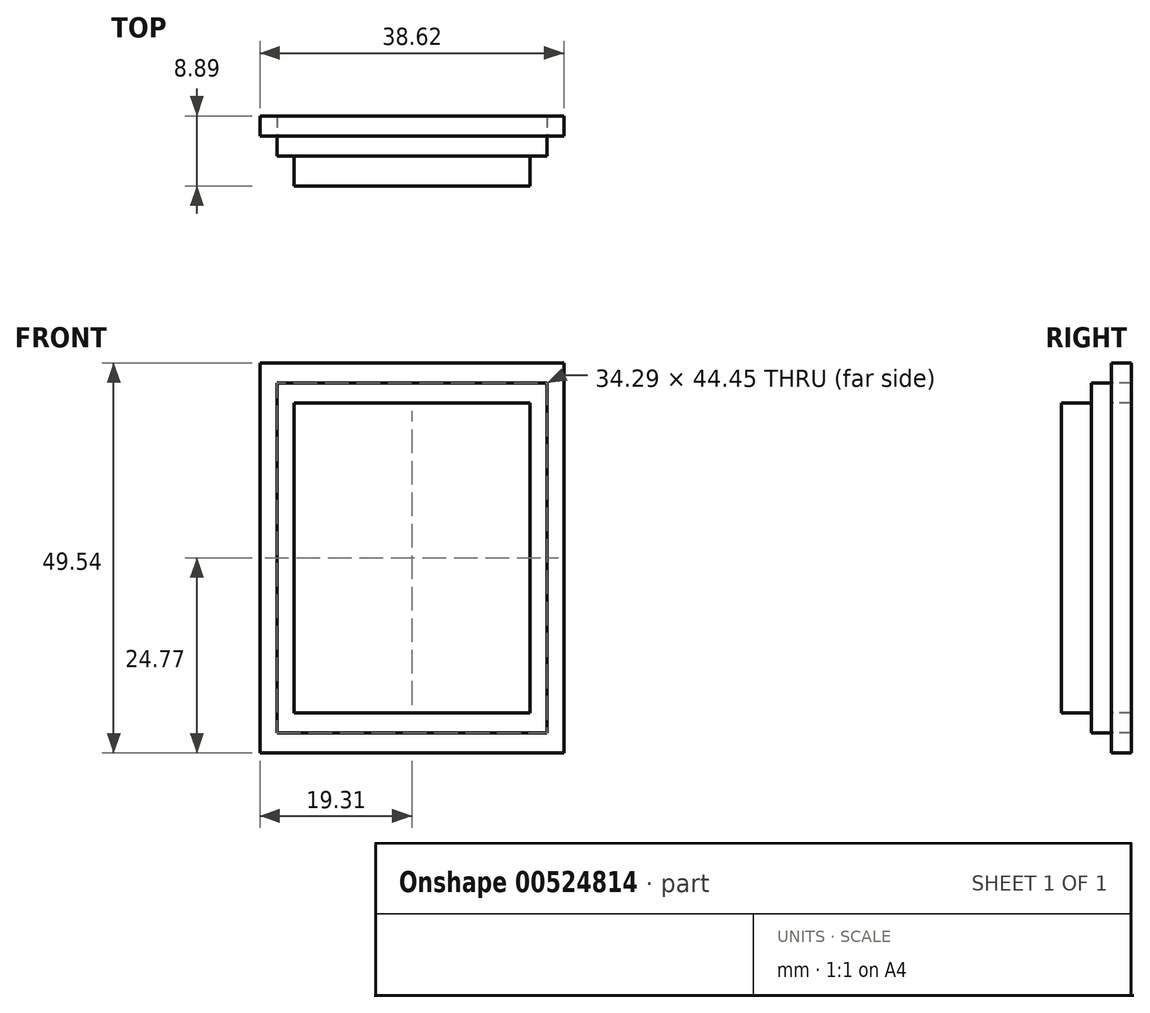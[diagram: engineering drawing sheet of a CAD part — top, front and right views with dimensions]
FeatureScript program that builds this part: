
annotation { "Feature Type Name" : "Feature", "Feature Type Description" : "" }
export const myFeature = defineFeature(function(context is Context, id is Id, definition is map)
    precondition{}
    {
        {
            var Q0;
            Q0=qCreatedBy(makeId("Front.planeOp"),FACE);
            var sketch = newSketch(context, id + "F0", { "sketchPlane" : qUnion([Q0])});
            skLineSegment(sketch, "E0.bottom", {"start": v(17.14, -22.23) * mm, "end": v(-17.14, -22.23) * mm});
            skLineSegment(sketch, "E0.top", {"start": v(17.14, 22.23) * mm, "end": v(-17.14, 22.23) * mm});
            skLineSegment(sketch, "E0.left", {"start": v(17.14, -22.23) * mm, "end": v(17.14, 22.23) * mm});
            skLineSegment(sketch, "E0.right", {"start": v(-17.14, -22.23) * mm, "end": v(-17.14, 22.23) * mm});
            skPoint(sketch, "E0.middle", {"position": v(0, 0) * mm});
            skLineSegment(sketch, "E1.bottom", {"start": v(-14.98, -22.23) * mm, "end": v(-19.31, -22.23) * mm});
            skLineSegment(sketch, "E1.top", {"start": v(-14.98, 22.23) * mm, "end": v(-19.31, 22.23) * mm});
            skLineSegment(sketch, "E1.left", {"start": v(-14.98, -22.23) * mm, "end": v(-14.98, 22.23) * mm});
            skLineSegment(sketch, "E1.right", {"start": v(-19.31, -22.23) * mm, "end": v(-19.31, 22.23) * mm});
            skPoint(sketch, "E1.middle", {"position": v(-17.14, 0) * mm});
            skLineSegment(sketch, "E2.bottom", {"start": v(19.31, -22.23) * mm, "end": v(14.98, -22.23) * mm});
            skLineSegment(sketch, "E2.top", {"start": v(19.31, 22.23) * mm, "end": v(14.98, 22.23) * mm});
            skLineSegment(sketch, "E2.left", {"start": v(19.31, -22.23) * mm, "end": v(19.31, 22.23) * mm});
            skLineSegment(sketch, "E2.right", {"start": v(14.98, -22.23) * mm, "end": v(14.98, 22.23) * mm});
            skPoint(sketch, "E2.middle", {"position": v(17.15, 0) * mm});
            skLineSegment(sketch, "E3.bottom", {"start": v(19.31, 19.69) * mm, "end": v(-19.31, 19.69) * mm});
            skLineSegment(sketch, "E3.top", {"start": v(19.31, 24.77) * mm, "end": v(-19.31, 24.77) * mm});
            skLineSegment(sketch, "E3.left", {"start": v(19.31, 19.69) * mm, "end": v(19.31, 24.77) * mm});
            skLineSegment(sketch, "E3.right", {"start": v(-19.31, 19.69) * mm, "end": v(-19.31, 24.77) * mm});
            skPoint(sketch, "E3.middle", {"position": v(0, 22.23) * mm});
            skLineSegment(sketch, "E4.bottom", {"start": v(19.31, -24.77) * mm, "end": v(-19.31, -24.77) * mm});
            skLineSegment(sketch, "E4.top", {"start": v(19.31, -19.68) * mm, "end": v(-19.31, -19.68) * mm});
            skLineSegment(sketch, "E4.left", {"start": v(19.31, -24.77) * mm, "end": v(19.31, -19.68) * mm});
            skLineSegment(sketch, "E4.right", {"start": v(-19.31, -24.77) * mm, "end": v(-19.31, -19.68) * mm});
            skPoint(sketch, "E4.middle", {"position": v(0, -22.23) * mm});
            skSolve(sketch);
        }
        {
            var Q0;
            {var subQ0=sQuery(id+"F0.wireOp",EDGE,"E4.top");var subQ1=sQuery(id+"F0.wireOp",EDGE,"E1.left");var subQ2=makeQuery(id+"F0.imprint","INTERSECT",VERTEX,{"derivedFrom":[subQ1,subQ0]});Q0=makeQuery(id+"F0.imprint","IMPRINT",FACE,{"disambiguationData":[TD([[makeQuery(id+"F0.imprint","IMPRINT",EDGE,{"disambiguationData":[TD([[subQ2,-1.0]])],"derivedFrom":subQ1}),-1.0]])]});}
            extrude(context, id + "F1", {"entities" : qUnion([Q0]), "depth" : 6.35 * mm, "offsetDistance" : 25.4 * mm});
        }
        {
            var Q0;
            Q0 = qSketchRegion(id + "F0", true);
            extrude(context, id + "F2", {"entities" : qUnion([Q0]), "oppositeDirection" : true, "depth" : 2.54 * mm, "offsetDistance" : 25.4 * mm});
        }
        {
            var Q0;
            {var subQ0=sQuery(id+"F0.wireOp",EDGE,"E0.top");Q0=makeQuery(id+"F0.imprint","IMPRINT",FACE,{"disambiguationData":[TD([[makeQuery(id+"F0.imprint","IMPRINT",EDGE,{"derivedFrom":subQ0}),1.0]])]});}
            var Q1;
            {var subQ0=sQuery(id+"F0.wireOp",EDGE,"E4.top");var subQ1=sQuery(id+"F0.wireOp",EDGE,"E0.left");var subQ2=makeQuery(id+"F0.imprint","INTERSECT",VERTEX,{"derivedFrom":[subQ1,subQ0]});Q1=makeQuery(id+"F0.imprint","IMPRINT",FACE,{"disambiguationData":[TD([[makeQuery(id+"F0.imprint","IMPRINT",EDGE,{"disambiguationData":[TD([[subQ2,-1.0]])],"derivedFrom":subQ1}),1.0]])]});}
            var Q2;
            {var subQ0=sQuery(id+"F0.wireOp",EDGE,"E0.bottom");Q2=makeQuery(id+"F0.imprint","IMPRINT",FACE,{"disambiguationData":[TD([[makeQuery(id+"F0.imprint","IMPRINT",EDGE,{"derivedFrom":subQ0}),-1.0]])]});}
            var Q3;
            {var subQ0=sQuery(id+"F0.wireOp",EDGE,"E4.top");var subQ1=sQuery(id+"F0.wireOp",EDGE,"E0.right");var subQ2=makeQuery(id+"F0.imprint","INTERSECT",VERTEX,{"derivedFrom":[subQ1,subQ0]});Q3=makeQuery(id+"F0.imprint","IMPRINT",FACE,{"disambiguationData":[TD([[makeQuery(id+"F0.imprint","IMPRINT",EDGE,{"disambiguationData":[TD([[subQ2,-1.0]])],"derivedFrom":subQ1}),-1.0]])]});}
            extrude(context, id + "F3", {"entities" : qUnion([Q0, Q1, Q2, Q3]), "operationType" : NewBodyOperationType.ADD, "depth" : 2.54 * mm, "offsetDistance" : 25.4 * mm});
        }
    });
